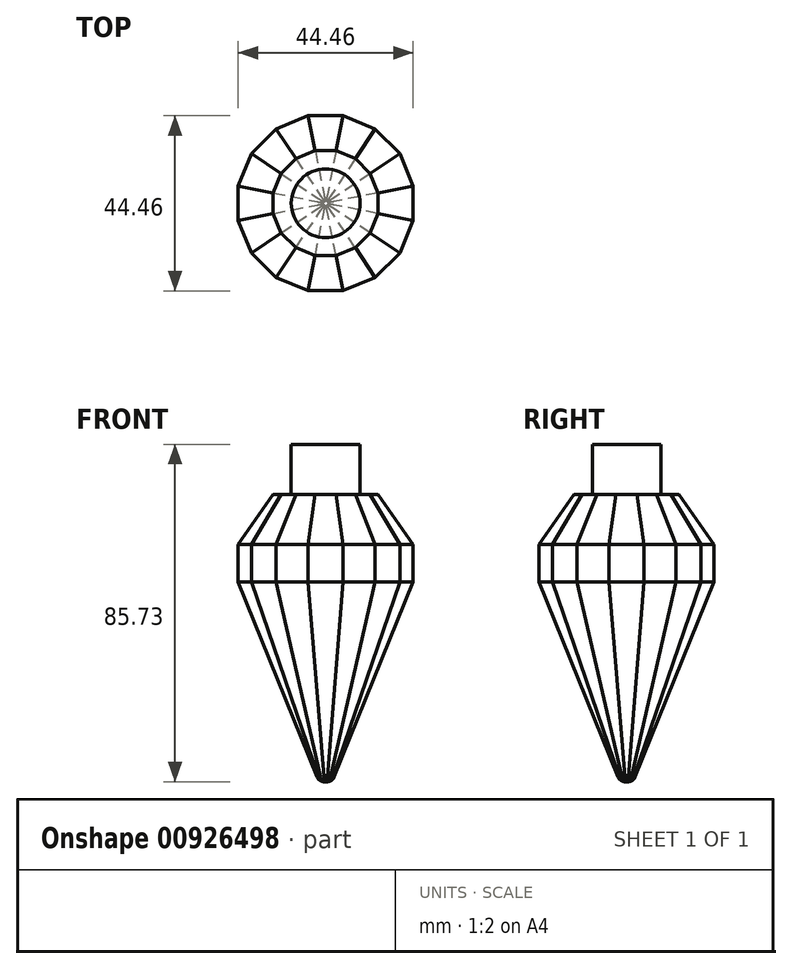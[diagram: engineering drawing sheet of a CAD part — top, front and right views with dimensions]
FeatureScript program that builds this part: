
annotation { "Feature Type Name" : "Feature", "Feature Type Description" : "" }
export const myFeature = defineFeature(function(context is Context, id is Id, definition is map)
    precondition{}
    {
        {
            var Q0;
            Q0=qCreatedBy(makeId("Top.planeOp"),FACE);
            var sketch = newSketch(context, id + "F0", { "sketchPlane" : qUnion([Q0])});
            skCircle(sketch, "E0.cCircle", {"center": v(0, 0) * mm, "radius": 22.23 * mm, "construction": true});
            skLineSegment(sketch, "E0.0", {"start": v(18.84, -12.59) * mm, "end": v(12.59, -18.84) * mm});
            skLineSegment(sketch, "E0.1", {"start": v(12.59, -18.84) * mm, "end": v(4.42, -22.23) * mm});
            skLineSegment(sketch, "E0.2", {"start": v(4.42, -22.23) * mm, "end": v(-4.42, -22.23) * mm});
            skLineSegment(sketch, "E0.3", {"start": v(-4.42, -22.22) * mm, "end": v(-12.59, -18.84) * mm});
            skLineSegment(sketch, "E0.4", {"start": v(-12.59, -18.84) * mm, "end": v(-18.84, -12.59) * mm});
            skLineSegment(sketch, "E0.5", {"start": v(-18.84, -12.59) * mm, "end": v(-22.23, -4.42) * mm});
            skLineSegment(sketch, "E0.6", {"start": v(-22.23, -4.42) * mm, "end": v(-22.23, 4.42) * mm});
            skLineSegment(sketch, "E0.7", {"start": v(-22.22, 4.42) * mm, "end": v(-18.84, 12.59) * mm});
            skLineSegment(sketch, "E0.8", {"start": v(-18.84, 12.59) * mm, "end": v(-12.59, 18.84) * mm});
            skLineSegment(sketch, "E0.9", {"start": v(-12.59, 18.84) * mm, "end": v(-4.42, 22.23) * mm});
            skLineSegment(sketch, "E0.10", {"start": v(-4.42, 22.23) * mm, "end": v(4.42, 22.22) * mm});
            skLineSegment(sketch, "E0.11", {"start": v(4.42, 22.22) * mm, "end": v(12.59, 18.84) * mm});
            skLineSegment(sketch, "E0.12", {"start": v(12.59, 18.84) * mm, "end": v(18.84, 12.59) * mm});
            skLineSegment(sketch, "E0.13", {"start": v(18.84, 12.59) * mm, "end": v(22.23, 4.42) * mm});
            skLineSegment(sketch, "E0.14", {"start": v(22.23, 4.42) * mm, "end": v(22.22, -4.42) * mm});
            skLineSegment(sketch, "E0.15", {"start": v(22.22, -4.42) * mm, "end": v(18.84, -12.59) * mm});
            skPoint(sketch, "E0.0.midPoint", {"position": v(15.72, -15.72) * mm});
            skSolve(sketch);
        }
        {
            var Q0;
            Q0 = qSketchRegion(id + "F0", true);
            extrude(context, id + "F1", {"entities" : qUnion([Q0]), "depth" : 9.52 * mm, "offsetDistance" : 25.4 * mm, "hasSecondDirection" : true, "secondDirectionOppositeDirection" : true, "secondDirectionDepth" : 50.8 * mm, "hasSecondDirectionDraft" : true, "secondDirectionDraftAngle" : 22 * degree, "secondDirectionDraftPullDirection" : true});
        }
        {
            var Q0;
            Q0=makeQuery(id+"F1.opExtrude","CAP_FACE",FACE,{"disambiguationData":[OSD([sQuery(id+"F0.wireOp",EDGE,"E0.0"),sQuery(id+"F0.wireOp",EDGE,"E0.1"),sQuery(id+"F0.wireOp",EDGE,"E0.2"),sQuery(id+"F0.wireOp",EDGE,"E0.3"),sQuery(id+"F0.wireOp",EDGE,"E0.4"),sQuery(id+"F0.wireOp",EDGE,"E0.5"),sQuery(id+"F0.wireOp",EDGE,"E0.6"),sQuery(id+"F0.wireOp",EDGE,"E0.7"),sQuery(id+"F0.wireOp",EDGE,"E0.8"),sQuery(id+"F0.wireOp",EDGE,"E0.9"),sQuery(id+"F0.wireOp",EDGE,"E0.10"),sQuery(id+"F0.wireOp",EDGE,"E0.11"),sQuery(id+"F0.wireOp",EDGE,"E0.12"),sQuery(id+"F0.wireOp",EDGE,"E0.13"),sQuery(id+"F0.wireOp",EDGE,"E0.14"),sQuery(id+"F0.wireOp",EDGE,"E0.15")])],"isStart":true});
            fillet(context, id + "F2", {"entities" : qUnion([Q0]), "radius" : 1.9 * mm, "tangentPropagation" : true, "allowEdgeOverflow" : false});
        }
        {
            var Q0;
            Q0=makeQuery(id+"F1.opExtrude","CAP_FACE",FACE,{"disambiguationData":[OSD([sQuery(id+"F0.wireOp",EDGE,"E0.0"),sQuery(id+"F0.wireOp",EDGE,"E0.1"),sQuery(id+"F0.wireOp",EDGE,"E0.2"),sQuery(id+"F0.wireOp",EDGE,"E0.3"),sQuery(id+"F0.wireOp",EDGE,"E0.4"),sQuery(id+"F0.wireOp",EDGE,"E0.5"),sQuery(id+"F0.wireOp",EDGE,"E0.6"),sQuery(id+"F0.wireOp",EDGE,"E0.7"),sQuery(id+"F0.wireOp",EDGE,"E0.8"),sQuery(id+"F0.wireOp",EDGE,"E0.9"),sQuery(id+"F0.wireOp",EDGE,"E0.10"),sQuery(id+"F0.wireOp",EDGE,"E0.11"),sQuery(id+"F0.wireOp",EDGE,"E0.12"),sQuery(id+"F0.wireOp",EDGE,"E0.13"),sQuery(id+"F0.wireOp",EDGE,"E0.14"),sQuery(id+"F0.wireOp",EDGE,"E0.15")])],"isStart":false});
            extrude(context, id + "F3", {"entities" : qUnion([Q0]), "operationType" : NewBodyOperationType.ADD, "depth" : 12.7 * mm, "offsetDistance" : 25.4 * mm, "hasDraft" : true, "draftAngle" : 35 * degree, "draftPullDirection" : true});
        }
        {
            var Q0;
            Q0=makeQuery(id+"F3.opExtrude","CAP_FACE",FACE,{"disambiguationData":[OSD([sQuery(id+"F0.wireOp",EDGE,"E0.0"),sQuery(id+"F0.wireOp",EDGE,"E0.1"),sQuery(id+"F0.wireOp",EDGE,"E0.2"),sQuery(id+"F0.wireOp",EDGE,"E0.3"),sQuery(id+"F0.wireOp",EDGE,"E0.4"),sQuery(id+"F0.wireOp",EDGE,"E0.5"),sQuery(id+"F0.wireOp",EDGE,"E0.6"),sQuery(id+"F0.wireOp",EDGE,"E0.7"),sQuery(id+"F0.wireOp",EDGE,"E0.8"),sQuery(id+"F0.wireOp",EDGE,"E0.9"),sQuery(id+"F0.wireOp",EDGE,"E0.10"),sQuery(id+"F0.wireOp",EDGE,"E0.11"),sQuery(id+"F0.wireOp",EDGE,"E0.12"),sQuery(id+"F0.wireOp",EDGE,"E0.13"),sQuery(id+"F0.wireOp",EDGE,"E0.14"),sQuery(id+"F0.wireOp",EDGE,"E0.15")])],"isStart":false});
            var sketch = newSketch(context, id + "F4", { "sketchPlane" : qUnion([Q0])});
            skCircle(sketch, "E1", {"center": v(0, 0) * mm, "radius": 8.73 * mm});
            skSolve(sketch);
        }
        {
            var Q0;
            Q0=makeQuery(id+"F4.imprint","IMPRINT",FACE,{"disambiguationData":[TD([[makeQuery(id+"F4.imprint","IMPRINT",EDGE,{"derivedFrom":sQuery(id+"F4.wireOp",EDGE,"E1")}),1.0]])]});
            extrude(context, id + "F5", {"entities" : qUnion([Q0]), "operationType" : NewBodyOperationType.ADD, "depth" : 12.7 * mm, "offsetDistance" : 25.4 * mm});
        }
    });
